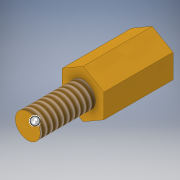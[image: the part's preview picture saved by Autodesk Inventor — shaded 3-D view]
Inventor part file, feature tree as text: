
AUTODESK INVENTOR PART (.ipt)
format: ipt  version: 2019 (Build 230136000, 136)  size: 141,312 bytes
history: native  units: mm
features: other x6, thread x2, extrude x2, hole x1, sketch x1
ambient origin geometry x8: Origin, YZ Plane, XZ Plane, XY Plane, X Axis, Y Axis, Z Axis, Center Point
bodies: Solid1 (feature_tree)
feature tree (12):
  other  "Table"
  thread  "Thread1:Designation = M2x0.4"  [1 undecoded]
  other  "d1 = 5 mm"
  other  "d1 = 10mm"
  other  "d1 = 15mm"
  other  "d1 = 20mm"
  other  "d1 = 25mm"
  extrude  "Hexagon1"  Depth=4.0mm TaperAngle=0.0deg
  hole  "Hole1"  [1 undecoded]
  extrude  "Extrusion2"  Depth=2.999912mm
  thread  "Thread3"  [1 undecoded]
  sketch  "Sketch1"  dims[d1=5.0mm d2=0.0mm d17=10.0mm d18=10.0mm d5=1.567mm d6=4.0mm d7=4.4mm d8=2.0mm d9=90.0deg d10=4.0mm d11=0.0mm d13=4.0mm d14=0.0mm d19=0.0mm d20=2.999912mm d21=1.732mm d22=1.8mm d25=10.0mm d26=0.0mm]
note: 3 required parameter values undecoded (feature->parameter linkage not recoverable at this tier; creation-order binding heuristic only, values carry confidence <= 0.55)
